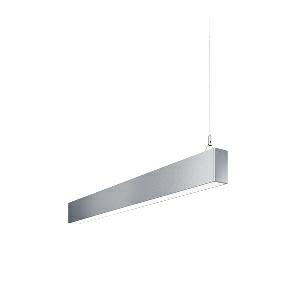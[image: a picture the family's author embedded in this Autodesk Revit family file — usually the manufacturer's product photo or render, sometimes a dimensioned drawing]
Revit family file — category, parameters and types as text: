
# Revit family: idoo_line_-_ilp_2000_840_d_end_00805685_139a
name_source: partatom
category: Lighting Fixtures
units: mm (PartAtom-declared; Revit-internal decimal feet)

## family parameters
Cut with Voids When Loaded = No
Host = Face
Light Source = No
Part Type = Normal
Room Calculation Point = No
Round Connector Dimension = Use Diameter
Shared = No

## types (1)
- IDOO.line - ILP 2000/840/D END (1 x LED, 2350 lm, 4000K)
    Apparent Load = 17 VA
    Approval mark = CE
    CIE Flux Codes = 66 91 98 40 100
    Color Rendering = 80-89
    Color Temperature = 4000K
    Control Gear = Electronic ballast
    Default Elevation = 1800 mm
    Description = ILP 2000/840/D|Suspended luminaire|light source: LED|connected load: 220-240 V, 50/60 Hz|Power consumption: approx. 17 W|standby: approx. 0,20|luminous flux: 2350 lm|luminous efficacy: 138 lm/W|light distribution: Direct/indirect|direct ratio: approx. 40 %|colour temperature: Cold white, ca. 4000 K|color rendering index (CRI): >= 80|chromaticity tolerance:  3 SDCM|System of protection: IP 40|technology: Continuously dimmable|luminaire body|material: Sectional aluminium|colour: Silver|lamp cover: Acrylic (PMMA), Clear|mains lead: 1,0 m With free stranded wires|Fastening: Steel cable 0.3 - 0.7 m|glare control: Prism aperture|luminance(L65): <= 2700 cd/m|unified glare rating(4H 8H): <=  16|special features: DALI Load 1x, TouchDIM - dimming via standard switch, Through-wired, up to 18 m on one mains connection, Flicker-free, Suitable as emergency lighting, Mechanical and electrical connection of the individual modules without tools|
    Frequency = 50 Hz
    Height = 110 mm
    Lamp = 1 x LED
    Lamp Light Flux = 2350 lm
    Lamp count = 1
    Length = 848 mm
    Luminous efficacy = 138 lm/W
    Manufacturer = Waldmann
    ModVariant = No
    Model = 00805685
    Mounting Place = Ceiling
    Mounting Type = Pendant
    Number of Poles = 1
    OnlyDefault = Yes
    Power Factor = 1
    Product Name = IDOO.line - ILP 2000/840/D END
    Product group = Suspended luminaire
    ProductGroupID = 9
    Protection Class = Protection class I
    Protection Degree = IP 40
    RLX_Detail_Level = 1
    RLX_Emergency_Light_Flux = 0 lm
    RLX_Emergency_Type = 0
    RLX_Emergency_Type_DB = No
    RlxData = <blob elided: 18529 chars, md5=515b0da5>
    Socket = socket
    Standby Power = 0 W
    System Light Flux = 2350 lm
    System Power = 17 W
    Type Comments = Product without accessories
    Type Image = 113300000-00692564.jpg
    URL = http://relux.com
    VarID = ---
    Voltage = 230 V
    Voltage Range = 220-240 V
    Weight = 0.00 kg
    Width = 60 mm  [stored 0.19685 ft]

note: [stored X ft] marks values corroborated as IEEE doubles in the binary element streams (Revit-internal decimal feet)

## geometry (parser evidence)
native form markers: Blend x4, Sweep x14
no freeform markers — native parametric forms only
